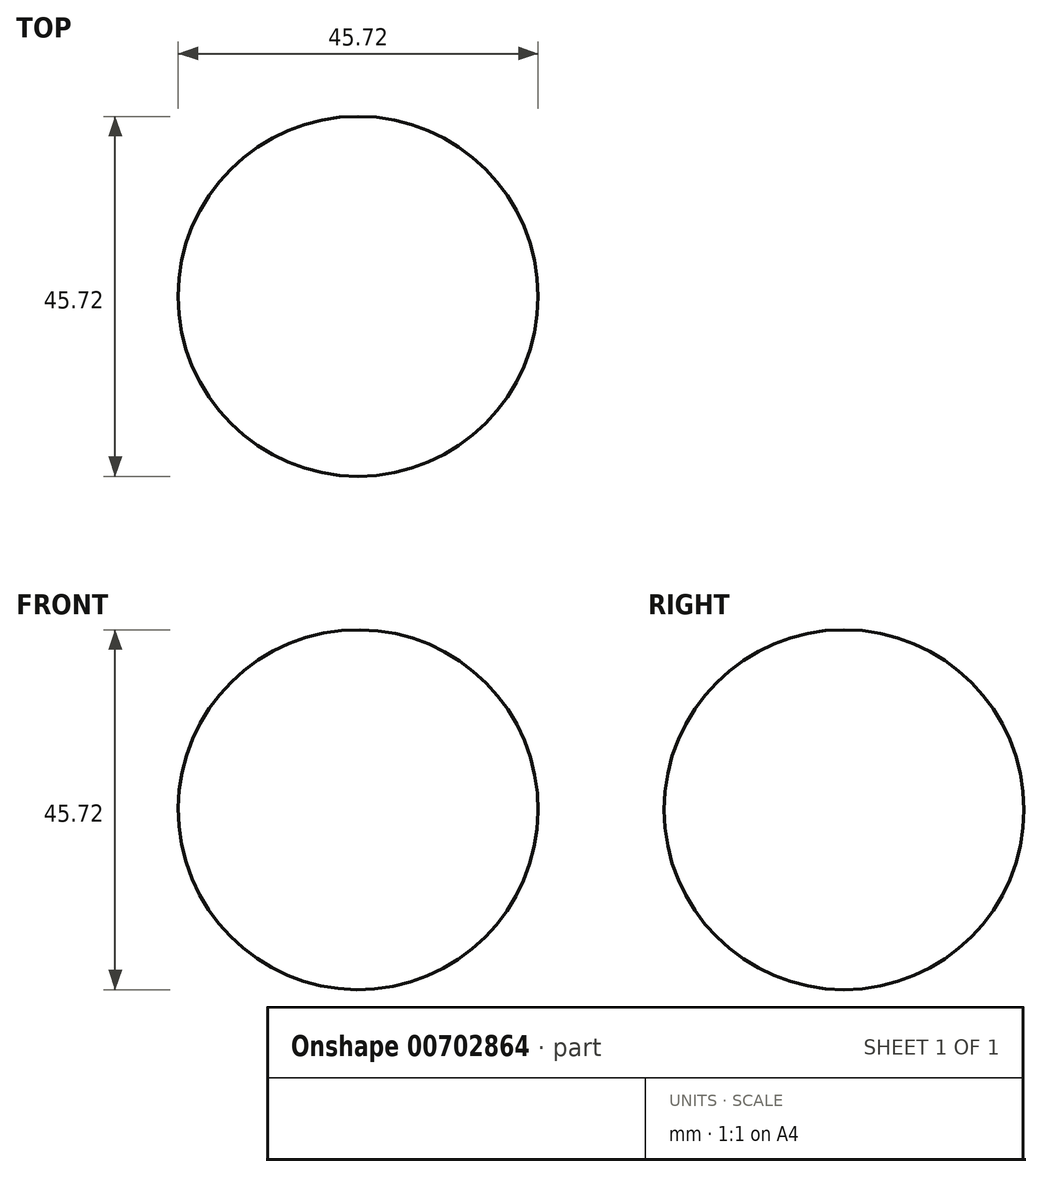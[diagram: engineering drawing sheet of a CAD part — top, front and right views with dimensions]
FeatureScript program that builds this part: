
annotation { "Feature Type Name" : "Feature", "Feature Type Description" : "" }
export const myFeature = defineFeature(function(context is Context, id is Id, definition is map)
    precondition{}
    {
        {
            var Q0;
            Q0=qCreatedBy(makeId("Front.planeOp"),FACE);
            var sketch = newSketch(context, id + "F0", { "sketchPlane" : qUnion([Q0])});
            skCircle(sketch, "E0", {"center": v(-15.51, 26.5) * mm, "radius": 22.86 * mm});
            skLineSegment(sketch, "E1", {"start": v(-15.51, 26.5) * mm, "end": v(-17.62, 49.26) * mm});
            skLineSegment(sketch, "E2", {"start": v(-15.51, 26.5) * mm, "end": v(-13.4, 3.73) * mm});
            skSolve(sketch);
        }
        {
            var Q0;
            {var subQ0=sQuery(id+"F0.wireOp",EDGE,"E1");Q0=makeQuery(id+"F0.imprint","IMPRINT",FACE,{"disambiguationData":[TD([[makeQuery(id+"F0.imprint","IMPRINT",EDGE,{"derivedFrom":subQ0}),-1.0]])]});}
            var Q1;
            Q1=sQuery(id+"F0.wireOp",EDGE,"E2");
            revolve(context, id + "F1", {"surfaceOperationType" : NewSurfaceOperationType.NEW, "entities" : qUnion([Q0]), "axis" : qUnion([Q1]), "revolveType" : RevolveType.SYMMETRIC, "angle" : 360 * degree});
        }
    });
